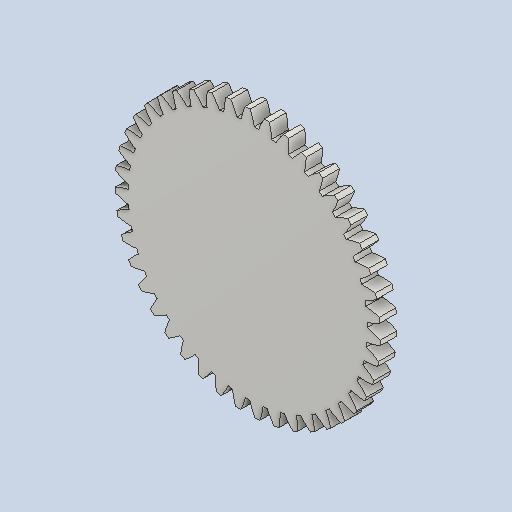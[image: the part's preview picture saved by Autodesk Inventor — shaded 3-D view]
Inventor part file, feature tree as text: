
AUTODESK INVENTOR PART (.ipt)
format: ipt  version: 2024 (Build 280153000, 153)  size: 308,224 bytes
history: native  units: mm (DEFAULTED — no unit token found)
features: plane x3, other x3, extrude x1, sketch x1
ambient origin geometry x8: Origin, YZ Plane, XZ Plane, XY Plane, X Axis, Y Axis, Z Axis, Center Point
bodies: Solid1 (feature_tree)
feature tree (8):
  extrude  "Extrusion1"  Depth=20.0mm TaperAngle=0.0deg
  plane  "Work Plane2"
  plane  "Work Plane8"
  plane  "Work Plane9"
  other  "Spur Gear"
  sketch  "Sketch1"  dims[d0=320.0mm d1=20.0mm d2=0.0mm d3=301.0mm d4=10.0mm d5=0.0mm d16=230.0mm d17=0.0mm d34=0.730603mm d39=0.0mm d41=0.0mm d43=230.0mm d46=230.0mm d47=0.0mm d48=0.0mm]
  other  "Srf1"
  other  "Pitch Diameter"
